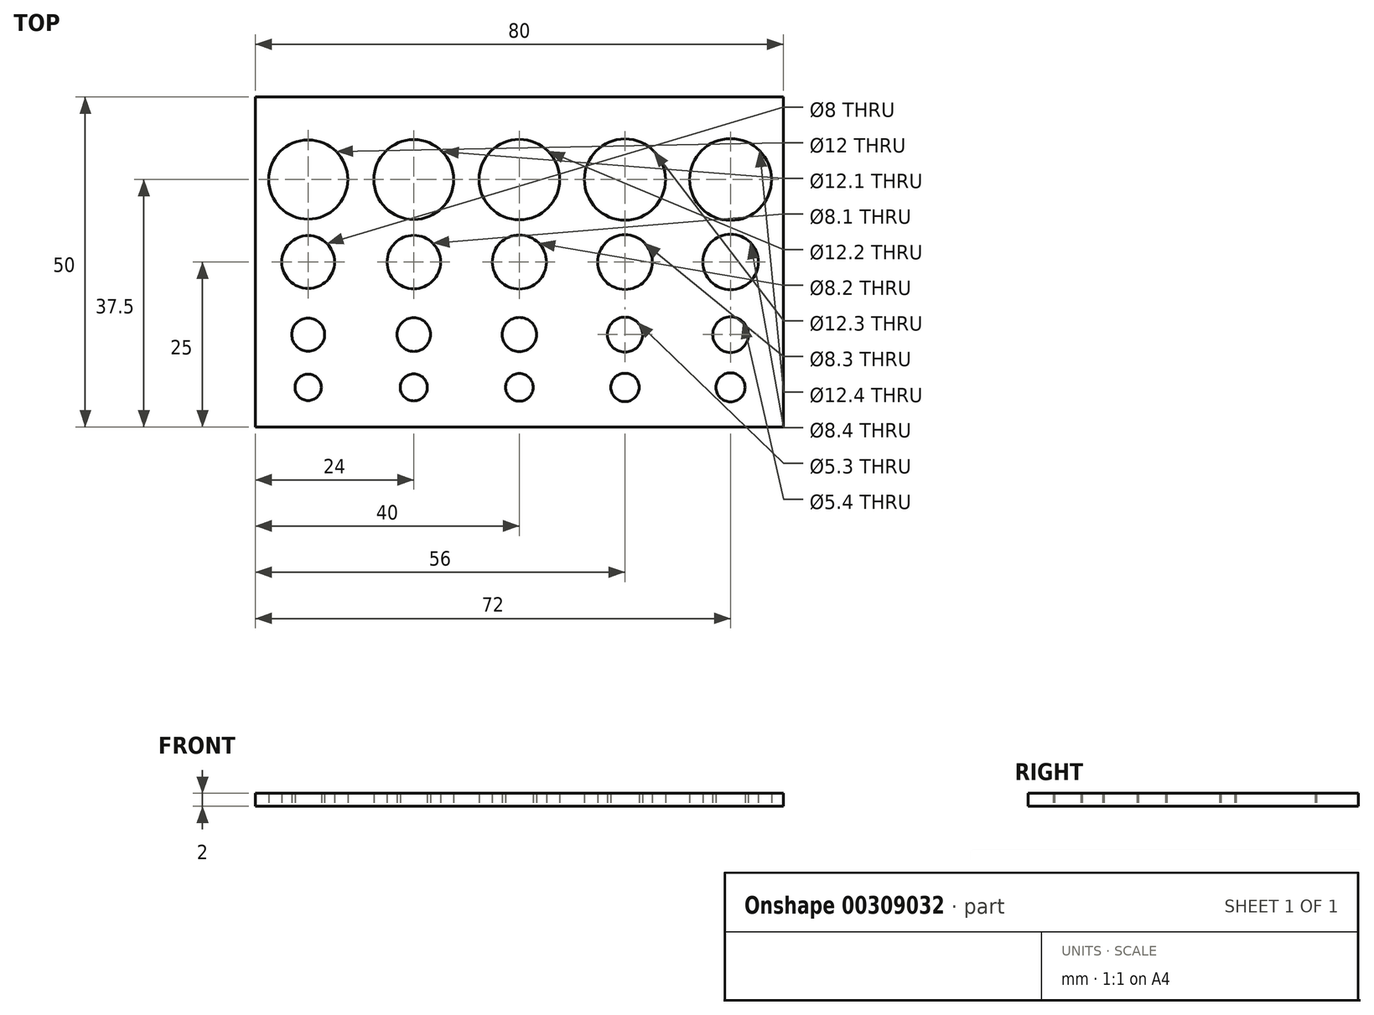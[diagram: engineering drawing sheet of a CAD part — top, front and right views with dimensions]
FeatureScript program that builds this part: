
annotation { "Feature Type Name" : "Feature", "Feature Type Description" : "" }
export const myFeature = defineFeature(function(context is Context, id is Id, definition is map)
    precondition{}
    {
        {
            var Q0;
            Q0=qCreatedBy(makeId("Top.planeOp"),FACE);
            var sketch = newSketch(context, id + "F0", { "sketchPlane" : qUnion([Q0])});
            skLineSegment(sketch, "E0.bottom", {"start": v(-40, 25) * mm, "end": v(40, 25) * mm});
            skLineSegment(sketch, "E0.top", {"start": v(-40, -25) * mm, "end": v(40, -25) * mm});
            skLineSegment(sketch, "E0.left", {"start": v(-40, 25) * mm, "end": v(-40, -25) * mm});
            skLineSegment(sketch, "E0.right", {"start": v(40, 25) * mm, "end": v(40, -25) * mm});
            skLineSegment(sketch, "E1", {"start": v(0, 0) * mm, "end": v(-40, 0) * mm, "construction": true});
            skLineSegment(sketch, "E2", {"start": v(0, 0) * mm, "end": v(0, -25) * mm, "construction": true});
            skLineSegment(sketch, "E3", {"start": v(-40, 12.5) * mm, "end": v(40, 12.5) * mm, "construction": true});
            skLineSegment(sketch, "E4", {"start": v(-40, -19) * mm, "end": v(40, -19) * mm, "construction": true});
            skPoint(sketch, "E4.endSnap0", {"position": v(0, -19) * mm});
            skLineSegment(sketch, "E5", {"start": v(0, 0) * mm, "end": v(40, 0) * mm, "construction": true});
            skLineSegment(sketch, "E6", {"start": v(0, 0) * mm, "end": v(0, 25) * mm, "construction": true});
            skPoint(sketch, "E7", {"position": v(0, 12.5) * mm});
            skCircle(sketch, "E8", {"center": v(-32, -19) * mm, "radius": 2 * mm});
            skCircle(sketch, "E9", {"center": v(-32, 0) * mm, "radius": 4 * mm});
            skCircle(sketch, "E10", {"center": v(-32, 12.5) * mm, "radius": 6 * mm});
            skLineSegment(sketch, "E11", {"start": v(-32, 25) * mm, "end": v(-32, -25) * mm, "construction": true});
            skLineSegment(sketch, "E12", {"start": v(-16, 25) * mm, "end": v(-16, -25) * mm, "construction": true});
            skLineSegment(sketch, "E13", {"start": v(16, 25) * mm, "end": v(16, -25) * mm, "construction": true});
            skLineSegment(sketch, "E14", {"start": v(32, 25) * mm, "end": v(32, -25) * mm, "construction": true});
            skCircle(sketch, "E15", {"center": v(-16, 12.5) * mm, "radius": 6.05 * mm});
            skCircle(sketch, "E16", {"center": v(-16, 0) * mm, "radius": 4.05 * mm});
            skCircle(sketch, "E17", {"center": v(-16, -19) * mm, "radius": 2.05 * mm});
            skCircle(sketch, "E18", {"center": v(0, 12.5) * mm, "radius": 6.1 * mm});
            skCircle(sketch, "E19", {"center": v(0, 0) * mm, "radius": 4.1 * mm});
            skCircle(sketch, "E20", {"center": v(0, -19) * mm, "radius": 2.1 * mm});
            skCircle(sketch, "E21", {"center": v(16, 12.5) * mm, "radius": 6.15 * mm});
            skCircle(sketch, "E22", {"center": v(16, 0) * mm, "radius": 4.15 * mm});
            skCircle(sketch, "E23", {"center": v(16, -19) * mm, "radius": 2.15 * mm});
            skCircle(sketch, "E24", {"center": v(32, 12.5) * mm, "radius": 6.2 * mm});
            skCircle(sketch, "E25", {"center": v(32, 0) * mm, "radius": 4.2 * mm});
            skCircle(sketch, "E26", {"center": v(32, -19) * mm, "radius": 2.2 * mm});
            skLineSegment(sketch, "E27", {"start": v(-40, -11) * mm, "end": v(40, -11) * mm, "construction": true});
            skCircle(sketch, "E28", {"center": v(-32, -11) * mm, "radius": 2.5 * mm});
            skCircle(sketch, "E29", {"center": v(-16, -11) * mm, "radius": 2.55 * mm});
            skCircle(sketch, "E30", {"center": v(0, -11) * mm, "radius": 2.6 * mm});
            skCircle(sketch, "E31", {"center": v(16, -11) * mm, "radius": 2.65 * mm});
            skCircle(sketch, "E32", {"center": v(32, -11) * mm, "radius": 2.7 * mm});
            skSolve(sketch);
        }
        {
            var Q0;
            Q0=makeQuery(id+"F0.imprint","IMPRINT",FACE,{"disambiguationData":[TD([[makeQuery(id+"F0.imprint","IMPRINT",EDGE,{"derivedFrom":sQuery(id+"F0.wireOp",EDGE,"E0.bottom")}),-1.0]])]});
            extrude(context, id + "F1", {"entities" : qUnion([Q0]), "depth" : 2 * mm, "offsetDistance" : 25 * mm});
        }
    });
